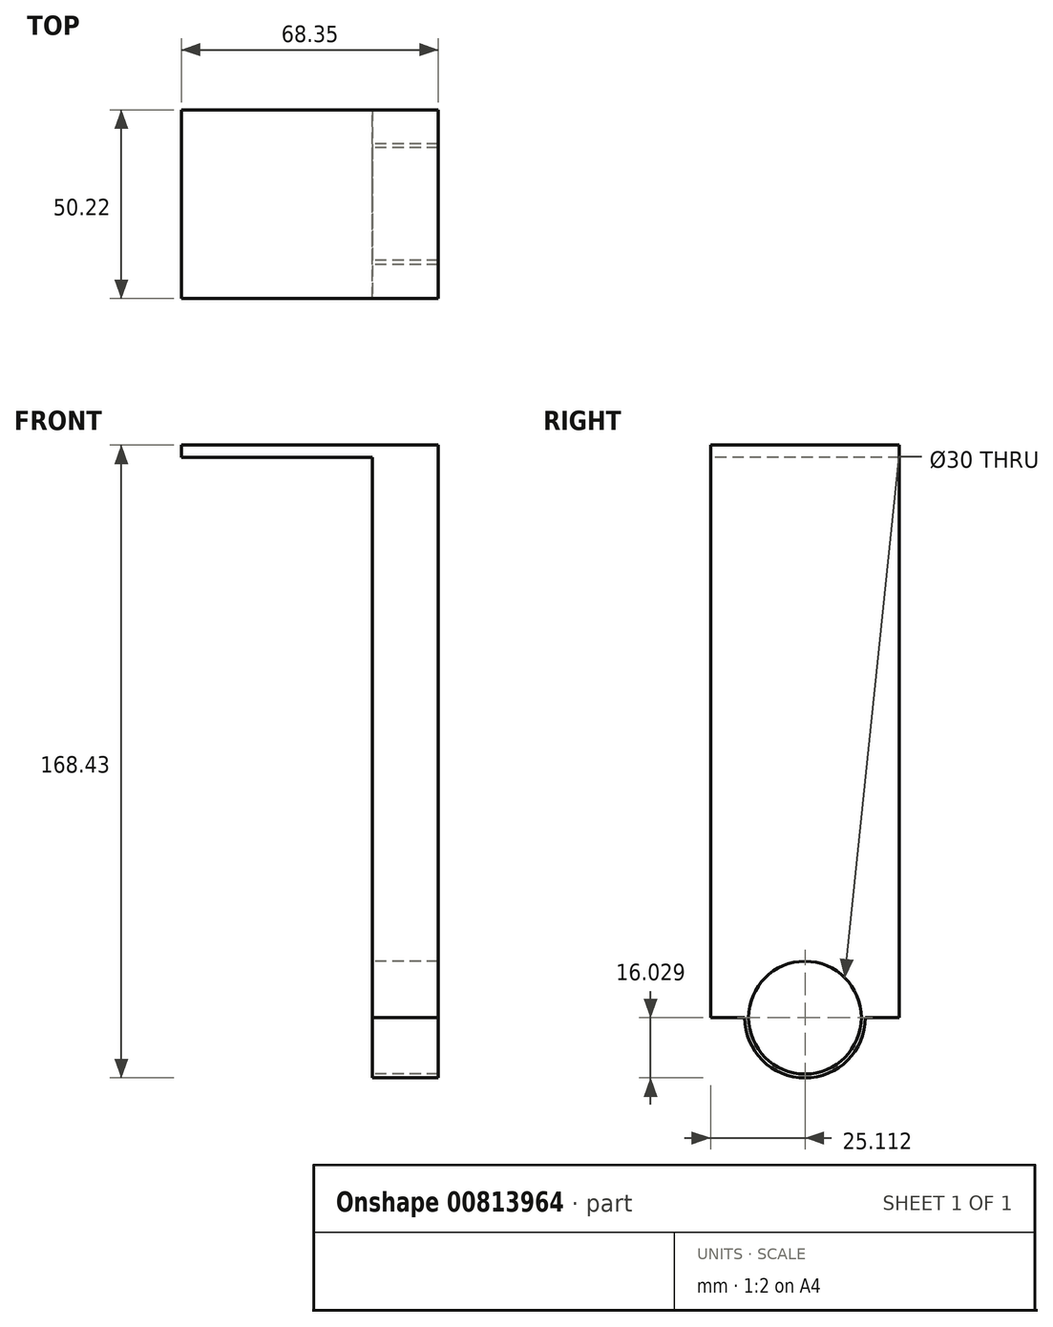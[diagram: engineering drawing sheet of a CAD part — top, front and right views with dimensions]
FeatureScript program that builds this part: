
annotation { "Feature Type Name" : "Feature", "Feature Type Description" : "" }
export const myFeature = defineFeature(function(context is Context, id is Id, definition is map)
    precondition{}
    {
        {
            var Q0;
            Q0=qCreatedBy(makeId("Right.planeOp"),FACE);
            var sketch = newSketch(context, id + "F0", { "sketchPlane" : qUnion([Q0])});
            skCircle(sketch, "E0", {"center": v(-46.45, 38.42) * mm, "radius": 15 * mm});
            skLineSegment(sketch, "E1.bottom", {"start": v(-71.56, 38.42) * mm, "end": v(-61.45, 38.42) * mm});
            skLineSegment(sketch, "E1.top", {"start": v(-71.56, 190.82) * mm, "end": v(-21.34, 190.82) * mm});
            skLineSegment(sketch, "E1.left", {"start": v(-71.56, 38.42) * mm, "end": v(-71.56, 190.82) * mm});
            skLineSegment(sketch, "E1.right", {"start": v(-21.34, 38.42) * mm, "end": v(-21.34, 190.82) * mm});
            skLineSegment(sketch, "E2.trimOffspring", {"start": v(-31.45, 38.42) * mm, "end": v(-21.34, 38.42) * mm});
            skCircle(sketch, "E3", {"center": v(-46.45, 38.42) * mm, "radius": 16.03 * mm});
            skSolve(sketch);
        }
        {
            var Q0;
            Q0=makeQuery(id+"F0.imprint","IMPRINT",FACE,{"disambiguationData":[TD([[makeQuery(id+"F0.imprint","IMPRINT",EDGE,{"derivedFrom":sQuery(id+"F0.wireOp",EDGE,"E1.top")}),-1.0]])]});
            var Q1;
            {var subQ0=sQuery(id+"F0.wireOp",EDGE,"E1.bottom");var subQ1=sQuery(id+"F0.wireOp",EDGE,"E0");var subQ2=makeQuery(id+"F0.imprint","INTERSECT",VERTEX,{"derivedFrom":[subQ1,subQ0]});Q1=makeQuery(id+"F0.imprint","IMPRINT",FACE,{"disambiguationData":[TD([[makeQuery(id+"F0.imprint","IMPRINT",EDGE,{"disambiguationData":[TD([[subQ2,1.0]])],"derivedFrom":subQ1}),-1.0]])]});}
            var Q2;
            {var subQ0=sQuery(id+"F0.wireOp",EDGE,"E1.bottom");var subQ1=sQuery(id+"F0.wireOp",EDGE,"E0");var subQ2=makeQuery(id+"F0.imprint","INTERSECT",VERTEX,{"derivedFrom":[subQ1,subQ0]});Q2=makeQuery(id+"F0.imprint","IMPRINT",FACE,{"disambiguationData":[TD([[makeQuery(id+"F0.imprint","IMPRINT",EDGE,{"disambiguationData":[TD([[subQ2,-1.0]])],"derivedFrom":subQ1}),-1.0]])]});}
            extrude(context, id + "F1", {"entities" : qUnion([Q0, Q1, Q2]), "depth" : 17.55 * mm, "offsetDistance" : 25.4 * mm});
        }
        {
            var Q0;
            Q0=makeQuery(id+"F1.opExtrude","CAP_FACE",FACE,{"disambiguationData":[OSD([sQuery(id+"F0.wireOp",EDGE,"E0"),sQuery(id+"F0.wireOp",EDGE,"E1.bottom"),sQuery(id+"F0.wireOp",EDGE,"E1.top"),sQuery(id+"F0.wireOp",EDGE,"E1.left"),sQuery(id+"F0.wireOp",EDGE,"E1.right"),sQuery(id+"F0.wireOp",EDGE,"E2.trimOffspring"),sQuery(id+"F0.wireOp",EDGE,"E3")])],"isStart":true});
            var sketch = newSketch(context, id + "F2", { "sketchPlane" : qUnion([Q0])});
            skLineSegment(sketch, "E4.bottom", {"start": v(21.34, 190.82) * mm, "end": v(71.56, 190.82) * mm});
            skLineSegment(sketch, "E4.top", {"start": v(21.34, 187.5) * mm, "end": v(71.56, 187.5) * mm});
            skLineSegment(sketch, "E4.left", {"start": v(21.34, 190.82) * mm, "end": v(21.34, 187.5) * mm});
            skLineSegment(sketch, "E4.right", {"start": v(71.56, 190.82) * mm, "end": v(71.56, 187.5) * mm});
            skSolve(sketch);
        }
        {
            var Q0;
            Q0=makeQuery(id+"F2.imprint","IMPRINT",FACE,{"disambiguationData":[TD([[makeQuery(id+"F2.imprint","IMPRINT",EDGE,{"derivedFrom":sQuery(id+"F2.wireOp",EDGE,"E4.bottom")}),1.0]])]});
            extrude(context, id + "F3", {"entities" : qUnion([Q0]), "operationType" : NewBodyOperationType.ADD, "depth" : 50.8 * mm, "offsetDistance" : 25.4 * mm});
        }
    });
